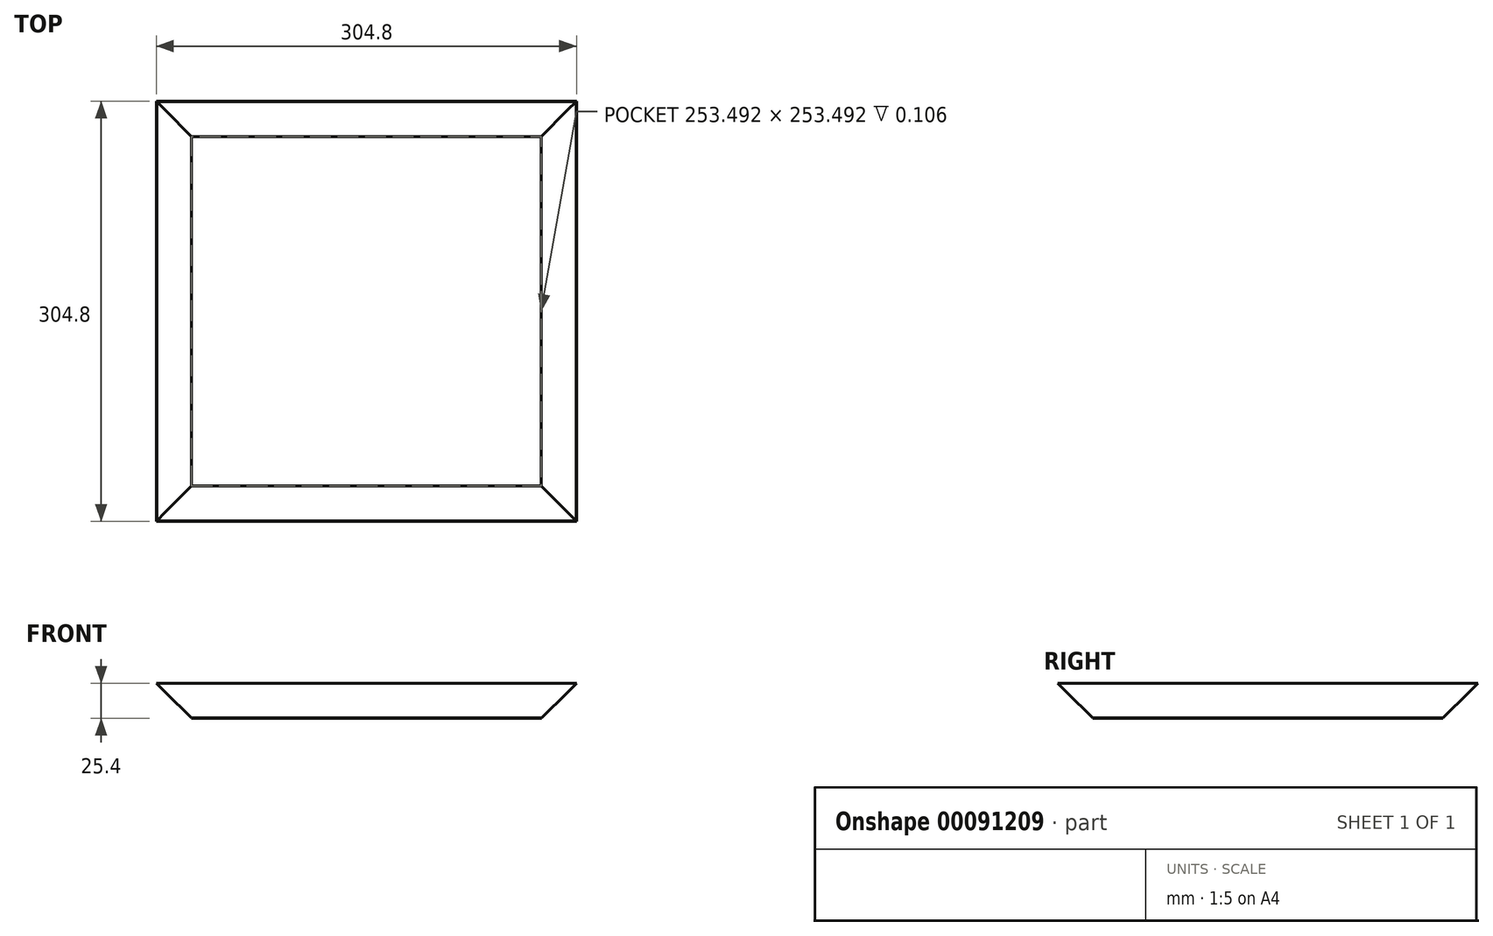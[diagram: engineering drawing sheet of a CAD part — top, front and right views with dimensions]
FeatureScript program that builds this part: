
annotation { "Feature Type Name" : "Feature", "Feature Type Description" : "" }
export const myFeature = defineFeature(function(context is Context, id is Id, definition is map)
    precondition{}
    {
        {
            var Q0;
            Q0=qCreatedBy(makeId("Top.planeOp"),FACE);
            var sketch = newSketch(context, id + "F0", { "sketchPlane" : qUnion([Q0])});
            skLineSegment(sketch, "E0.bottom", {"start": v(-127, 127) * mm, "end": v(127, 127) * mm});
            skLineSegment(sketch, "E0.top", {"start": v(-127, -127) * mm, "end": v(127, -127) * mm});
            skLineSegment(sketch, "E0.left", {"start": v(-127, 127) * mm, "end": v(-127, -127) * mm});
            skLineSegment(sketch, "E0.right", {"start": v(127, 127) * mm, "end": v(127, -127) * mm});
            skPoint(sketch, "E0.middle", {"position": v(0, 0) * mm});
            skSolve(sketch);
        }
        {
            var Q0;
            Q0 = qSketchRegion(id + "F0", true);
            extrude(context, id + "F1", {"entities" : qUnion([Q0]), "depth" : 0.25 * mm});
        }
        {
            var Q0;
            Q0=qCreatedBy(makeId("Top.planeOp"),FACE);
            cPlane(context, id + "F2", {"entities" : qUnion([Q0]), "cplaneType" : CPlaneType.OFFSET, "offset" : 19.05 * mm, "width" : 152.4 * mm, "height" : 152.4 * mm});
        }
        {
            var Q0;
            Q0=qCreatedBy(id+"F2.planeOp",FACE);
            var sketch = newSketch(context, id + "F3", { "sketchPlane" : qUnion([Q0])});
            skLineSegment(sketch, "E1.bottom", {"start": v(-146.05, -146.05) * mm, "end": v(146.05, -146.05) * mm});
            skLineSegment(sketch, "E1.top", {"start": v(-146.05, 146.05) * mm, "end": v(146.05, 146.05) * mm});
            skLineSegment(sketch, "E1.left", {"start": v(-146.05, -146.05) * mm, "end": v(-146.05, 146.05) * mm});
            skLineSegment(sketch, "E1.right", {"start": v(146.05, -146.05) * mm, "end": v(146.05, 146.05) * mm});
            skPoint(sketch, "E1.middle", {"position": v(0, 0) * mm});
            skSolve(sketch);
        }
        {
            var Q1;
            Q1=makeQuery(id+"F1.opExtrude","CAP_FACE",FACE,{"disambiguationData":[OSD([sQuery(id+"F0.wireOp",EDGE,"E0.bottom"),sQuery(id+"F0.wireOp",EDGE,"E0.top"),sQuery(id+"F0.wireOp",EDGE,"E0.left"),sQuery(id+"F0.wireOp",EDGE,"E0.right")])],"isStart":false});
            var Q2;
            Q2=makeQuery(id+"F3.imprint","IMPRINT",FACE,{"disambiguationData":[TD([[makeQuery(id+"F3.imprint","IMPRINT",EDGE,{"derivedFrom":sQuery(id+"F3.wireOp",EDGE,"E1.bottom")}),1.0]])]});
            loft(context, id + "F4", {"operationType" : NewBodyOperationType.ADD, "sheetProfilesArray" : [{ "sheetProfileEntities" : qUnion([Q1]) }, { "sheetProfileEntities" : qUnion([Q2]) }]});
        }
        {
            var Q0;
            Q0=qCreatedBy(id+"F2.planeOp",FACE);
            cPlane(context, id + "F5", {"entities" : qUnion([Q0]), "cplaneType" : CPlaneType.OFFSET, "offset" : 6.35 * mm, "width" : 152.4 * mm, "height" : 152.4 * mm});
        }
        {
            var Q0;
            Q0=qCreatedBy(id+"F5.planeOp",FACE);
            var sketch = newSketch(context, id + "F6", { "sketchPlane" : qUnion([Q0])});
            skLineSegment(sketch, "E2.bottom", {"start": v(-152.4, 152.4) * mm, "end": v(152.4, 152.4) * mm});
            skLineSegment(sketch, "E2.top", {"start": v(-152.4, -152.4) * mm, "end": v(152.4, -152.4) * mm});
            skLineSegment(sketch, "E2.left", {"start": v(-152.4, 152.4) * mm, "end": v(-152.4, -152.4) * mm});
            skLineSegment(sketch, "E2.right", {"start": v(152.4, 152.4) * mm, "end": v(152.4, -152.4) * mm});
            skPoint(sketch, "E2.middle", {"position": v(0, 0) * mm});
            skSolve(sketch);
        }
        {
            var Q1;
            Q1=makeQuery(id+"F4.opLoft","CAP_FACE",FACE,{"disambiguationData":[OSD([makeQuery(id+"F3.imprint","IMPRINT",FACE,{"disambiguationData":[TD([[makeQuery(id+"F3.imprint","IMPRINT",EDGE,{"derivedFrom":sQuery(id+"F3.wireOp",EDGE,"E1.bottom")}),1.0]])]})])],"isStart":true});
            var Q2;
            Q2=makeQuery(id+"F6.imprint","IMPRINT",FACE,{"disambiguationData":[TD([[makeQuery(id+"F6.imprint","IMPRINT",EDGE,{"derivedFrom":sQuery(id+"F6.wireOp",EDGE,"E2.bottom")}),-1.0]])]});
            loft(context, id + "F7", {"operationType" : NewBodyOperationType.ADD, "sheetProfilesArray" : [{ "sheetProfileEntities" : qUnion([Q1]) }, { "sheetProfileEntities" : qUnion([Q2]) }]});
        }
        {
            var Q0;
            Q0=makeQuery(id+"F7.opLoft","CAP_FACE",FACE,{"disambiguationData":[OSD([makeQuery(id+"F6.imprint","IMPRINT",FACE,{"disambiguationData":[TD([[makeQuery(id+"F6.imprint","IMPRINT",EDGE,{"derivedFrom":sQuery(id+"F6.wireOp",EDGE,"E2.bottom")}),-1.0]])]})])],"isStart":true});
            shell(context, id + "F8", {"entities" : qUnion([Q0]), "thickness" : 0.25 * mm});
        }
    });
